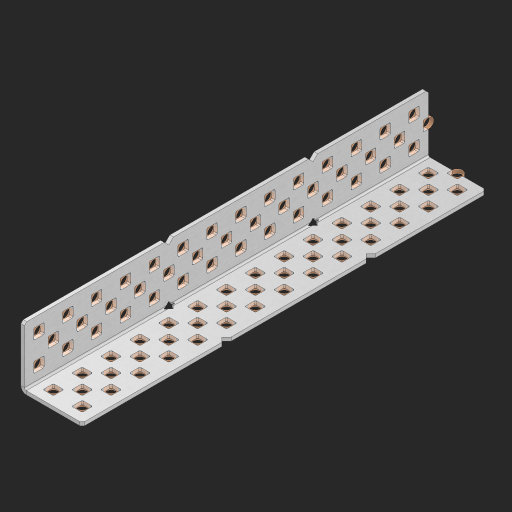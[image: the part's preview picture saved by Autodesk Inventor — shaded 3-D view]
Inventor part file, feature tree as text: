
AUTODESK INVENTOR PART (.ipt)
format: ipt  version: 2023 (Build 270158000, 158)  size: 1,209,344 bytes
history: native  units: in
note: dims shown in document units (in); Inventor stores cm internally (conversion verified against a paired STEP export)
features: other x90, extrude x82, sheet_metal_op x8, sketch x7, pattern_linear x2, mirror x1, chamfer x1
ambient origin geometry x8: Origin, YZ Plane, XZ Plane, XY Plane, X Axis, Y Axis, Z Axis, Center Point
bodies: Solid1 (feature_tree), Body (feature_tree)
feature tree (191):
  sheet_metal_op  "Flanges"
  sheet_metal_op  "Body Pattern"
  pattern_linear  "Center Pattern"  Spacing1=1.0in  [1 undecoded]
  other  "Arc Length"
  pattern_linear  "Notch Pattern"  Spacing1=0.25in  [1 undecoded]
  other  "Diagonal Plane"
  mirror  "Everything Mirrored"
  chamfer  "End Chamfer"
  sketch  "Sketch1"  dims[d0=1.0in]
  other  "Plate1"
  sketch  "Sketch2"  dims[d1=7.0in]
  other  "Plate2"
  sheet_metal_op  "Bend1"
  sheet_metal_op  "Corner1"
  sketch  "Sketch8"  dims[d2=0.0625in]
  sketch  "Sketch9"  dims[d3=0.0625in]
  other  "Srf91"
  sheet_metal_op  "Body Pattern Sketch"
  other  "Srf92"
  sketch  "Sketch13"  dims[d4=0.0312in]
  sketch  "Sketch15"  dims[d5=0.125in]
  sketch  "Sketch16"  dims[d6=0.0625in d7=1.0in d8=90.0deg d9=0.0312in d10=0.25in d11=0.0625in d12=0.0625in d49=0.182in d50=0.02in d52=0.25in d53=0.0625in d54=0.0in d55=0.172in d56=1.0in d57=0.0in d60=5.5118in d62=0.5in d63=0.7874in d65=0.5in d85=0.1473in d86=0.1782in d89=0.0625in d90=0.0in d91=0.04in d92=0.0491in d95=2.5in d96=0.04in d97=0.25in d98=45.0deg d99=0.25in d106=0.182in d107=0.02in d108=0.5in d110=0.0625in d111=0.0in d112=0.172in d113=0.5in d114=0.0in d117=0.5in d123=0.25in d125=0.25in d126=0.0491in d127=0.1473in d128=0.08in d129=0.04in d130=2.5in]
  other  "Srf786"
  other  "Srf856"
  other  "Srf857"
  other  "Srf858"
  other  "Srf859"
  other  "Srf860"
  other  "Srf861"
  other  "Srf889"
  other  "Srf890"
  other  "Srf891"
  other  "Srf1275"
  other  "Srf1276"
  other  "Srf1278"
  other  "Srf1279"
  other  "Srf1280"
  other  "Srf1281"
  other  "Srf1282"
  other  "Srf1283"
  other  "Srf1277"
  other  "Srf1285"
  other  "Srf1286"
  other  "Srf1287"
  other  "Srf1383"
  other  "Srf1384"
  other  "Srf1385"
  other  "Srf1386"
  other  "Srf1387"
  other  "Srf1388"
  other  "Srf1389"
  other  "Srf1390"
  other  "Srf1391"
  other  "Srf1392"
  other  "Srf1393"
  other  "Srf1394"
  other  "Srf1395"
  other  "Srf1396"
  other  "Srf1397"
  other  "Srf1398"
  other  "Srf1399"
  other  "Srf1400"
  other  "Srf1401"
  other  "Srf1402"
  other  "Srf1445"
  other  "Srf1446"
  other  "Srf1447"
  other  "Srf1448"
  other  "Srf1449"
  other  "Srf1450"
  other  "Srf1451"
  other  "Srf1452"
  other  "Srf1453"
  other  "Srf1454"
  other  "Srf1475"
  other  "Srf1476"
  other  "Srf1477"
  other  "Srf1478"
  other  "Srf1479"
  other  "Srf1480"
  other  "Srf1481"
  other  "Srf1482"
  other  "Srf1483"
  other  "Srf1484"
  other  "Srf1485"
  other  "Srf1486"
  other  "Srf1487"
  other  "Srf1488"
  other  "Srf1489"
  other  "Srf1490"
  other  "Srf1491"
  other  "Srf1492"
  other  "Srf1493"
  other  "Srf1494"
  other  "Srf1537"
  other  "Srf1538"
  other  "Srf1539"
  other  "Srf1540"
  other  "Srf1541"
  other  "Srf1542"
  other  "Srf1543"
  other  "Srf1544"
  other  "Srf1545"
  other  "Srf1546"
  sheet_metal_op  "Body Stamp"
  sheet_metal_op  "Body Circle"
  other  "Center Stamp"
  other  "Center Circle"
  sheet_metal_op  "Notch"
  extrude  "ExtrusionSrf92"  Depth=0.0625in
  extrude  "ExtrusionSrf856"  Depth=0.0625in
  extrude  "ExtrusionSrf857"  Depth=0.182in
  extrude  "ExtrusionSrf858"  Depth=0.02in
  extrude  "ExtrusionSrf859"  Depth=0.25in
  extrude  "ExtrusionSrf860"  Depth=0.0625in
  extrude  "ExtrusionSrf861"  TaperAngle=0.0deg  [1 undecoded]
  extrude  "ExtrusionSrf889"  Depth=2.5in
  extrude  "ExtrusionSrf890"  Depth=1.0in TaperAngle=0.0deg
  extrude  "ExtrusionSrf891"  Depth=2.5in
  extrude  "ExtrusionSrf1275"  Depth=0.5in
  extrude  "ExtrusionSrf1276"  Depth=2.5in
  extrude  "ExtrusionSrf1277"  Depth=2.5in
  extrude  "ExtrusionSrf1278"  Depth=0.0625in
  extrude  "ExtrusionSrf1279"  Depth=2.5in TaperAngle=0.0deg
  extrude  "ExtrusionSrf1280"  Depth=2.5in
  extrude  "ExtrusionSrf1281"  Depth=0.25in TaperAngle=45.0deg
  extrude  "ExtrusionSrf1282"  Depth=0.25in
  extrude  "ExtrusionSrf1345"  Depth=0.182in
  extrude  "ExtrusionSrf1346"  Depth=0.02in
  extrude  "ExtrusionSrf1347"  Depth=0.5in
  extrude  "ExtrusionSrf1348"  Depth=0.0625in
  extrude  "ExtrusionSrf1383"  TaperAngle=0.0deg  [1 undecoded]
  extrude  "ExtrusionSrf1384"  Depth=2.5in
  extrude  "ExtrusionSrf1385"  Depth=0.5in TaperAngle=0.0deg
  extrude  "ExtrusionSrf1386"  Depth=0.5in
  extrude  "ExtrusionSrf1387"  Depth=0.25in
  extrude  "ExtrusionSrf1388"  Depth=0.25in
  extrude  "ExtrusionSrf1389"  Depth=2.5in
  extrude  "ExtrusionSrf1390"  Depth=2.5in
  extrude  "ExtrusionSrf1391"  Depth=2.5in
  extrude  "ExtrusionSrf1392"  Depth=2.5in
  extrude  "ExtrusionSrf1393"  Depth=2.5in
  extrude  "ExtrusionSrf1394"  [1 undecoded]
  extrude  "ExtrusionSrf1395"  [1 undecoded]
  extrude  "ExtrusionSrf1396"  [1 undecoded]
  extrude  "ExtrusionSrf1397"  [1 undecoded]
  extrude  "ExtrusionSrf1398"  [1 undecoded]
  extrude  "ExtrusionSrf1399"  [1 undecoded]
  extrude  "ExtrusionSrf1400"  [1 undecoded]
  extrude  "ExtrusionSrf1401"  [1 undecoded]
  extrude  "ExtrusionSrf1402"  [1 undecoded]
  extrude  "ExtrusionSrf1445"  [1 undecoded]
  extrude  "ExtrusionSrf1446"  [1 undecoded]
  extrude  "ExtrusionSrf1447"  [1 undecoded]
  extrude  "ExtrusionSrf1448"  [1 undecoded]
  extrude  "ExtrusionSrf1449"  [1 undecoded]
  extrude  "ExtrusionSrf1450"  [1 undecoded]
  extrude  "ExtrusionSrf1451"  [1 undecoded]
  extrude  "ExtrusionSrf1452"  [1 undecoded]
  extrude  "ExtrusionSrf1453"  [1 undecoded]
  extrude  "ExtrusionSrf1454"  [1 undecoded]
  extrude  "ExtrusionSrf1475"  [1 undecoded]
  extrude  "ExtrusionSrf1476"  [1 undecoded]
  extrude  "ExtrusionSrf1477"  [1 undecoded]
  extrude  "ExtrusionSrf1478"  [1 undecoded]
  extrude  "ExtrusionSrf1479"  [1 undecoded]
  extrude  "ExtrusionSrf1480"  [1 undecoded]
  extrude  "ExtrusionSrf1481"  [1 undecoded]
  extrude  "ExtrusionSrf1482"  [1 undecoded]
  extrude  "ExtrusionSrf1483"  [1 undecoded]
  extrude  "ExtrusionSrf1484"  [1 undecoded]
  extrude  "ExtrusionSrf1485"  [1 undecoded]
  extrude  "ExtrusionSrf1486"  [1 undecoded]
  extrude  "ExtrusionSrf1487"  [1 undecoded]
  extrude  "ExtrusionSrf1488"  [1 undecoded]
  extrude  "ExtrusionSrf1489"  [1 undecoded]
  extrude  "ExtrusionSrf1490"  [1 undecoded]
  extrude  "ExtrusionSrf1491"  [1 undecoded]
  extrude  "ExtrusionSrf1492"  [1 undecoded]
  extrude  "ExtrusionSrf1493"  [1 undecoded]
  extrude  "ExtrusionSrf1494"  [1 undecoded]
  extrude  "ExtrusionSrf1537"  [1 undecoded]
  extrude  "ExtrusionSrf1538"  [1 undecoded]
  extrude  "ExtrusionSrf1539"  [1 undecoded]
  extrude  "ExtrusionSrf1540"  [1 undecoded]
  extrude  "ExtrusionSrf1541"  [1 undecoded]
  extrude  "ExtrusionSrf1542"  [1 undecoded]
  extrude  "ExtrusionSrf1543"  [1 undecoded]
  extrude  "ExtrusionSrf1544"  [1 undecoded]
  extrude  "ExtrusionSrf1545"  [1 undecoded]
  extrude  "ExtrusionSrf1546"  [1 undecoded]
note: 53 required parameter values undecoded (feature->parameter linkage not recoverable at this tier; creation-order binding heuristic only, values carry confidence <= 0.55)
